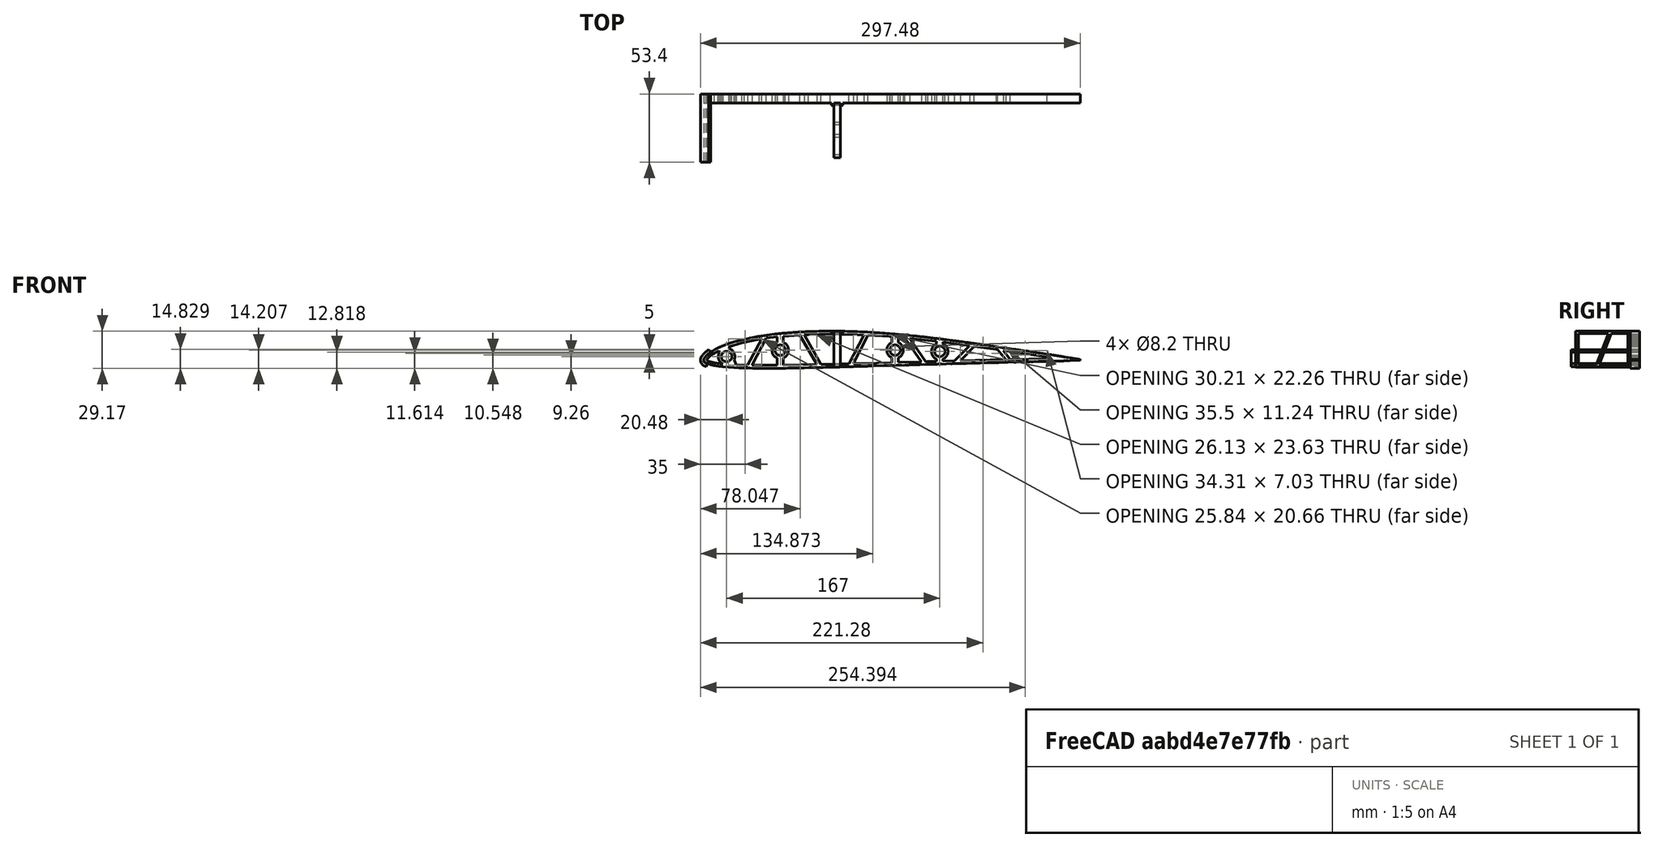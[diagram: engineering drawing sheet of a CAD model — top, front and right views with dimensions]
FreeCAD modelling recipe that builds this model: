
FCSTD DOCUMENT  (FreeCAD 1.0R39319 (Git))
Label: fpv_plane_wing
License: All rights reserved
LicenseURL: https://en.wikipedia.org/wiki/All_rights_reserved
objects: Sketcher::SketchObject×14, PartDesign::Pocket×9, PartDesign::Pad×5, Part::Part2DObjectPython×3, PartDesign::Body×3, App::DocumentObjectGroup×1, PartDesign::Thickness×1
note: 79 computed .brp shape members not serialized (recipe doc carries the construction recipe); baked Part::Feature solids carry a one-line shape summary decoded from their .brp

FEATURE [Part::Part2DObjectPython] Wire  # Draft 2D object (typed FeaturePython)
  Area = 0.0621999
  ChamferSize = 0
  Closed = true
  End = (1.00001,0,0)
  FilletRadius = 0
  Length = 2.02855
  MakeFace = true
  Placement = pos=(0,0,0) rot=(1,0,0;1.5708rad)
  Points = (61) [(1,0,0),(0.99663,0.00039,0),(0.98679,0.00172,0),(0.97104,0.00419,0),(0.94996,0.00769,0),(0.92398,0.01193,0),(0.89336,0.0167,0),(0.8584,0.02198,0),+53 more]
  Start = (1,0,0)
  Subdivisions = 0
FEATURE [Part::Part2DObjectPython] Wire002  label="wing_wire_300mm"  # Draft 2D object (typed FeaturePython)
  Area = 5597.99
  ChamferSize = 0
  Closed = true
  End = (300.003,0,0)
  FilletRadius = 0
  Length = 608.564
  MakeFace = true
  Placement = pos=(0,0,0) rot=(1,0,0;1.5708rad)
  Points = (61) [(300,0,0),(298.989,0.117,0),(296.037,0.516,0),(291.312,1.257,0),(284.988,2.307,0),(277.194,3.579,0),(268.008,5.01,0),(257.52,6.594,0),+53 more]
  Start = (300,0,0)
  Subdivisions = 0
FEATURE [App::DocumentObjectGroup] s3021
  Group = -> [Wire,Wire002]
FEATURE [Part::Part2DObjectPython] BSpline001  label="wing_wire_300mm001"  # Draft 2D object (typed FeaturePython)
  Area = 5612.28
  Closed = true
  MakeFace = true
  Parameterization = 1
  Placement = pos=(0,0,0) rot=(1,0,0;1.5708rad)
  Points = (61) [(300,0,0),(298.989,0.117,0),(296.037,0.516,0),(291.312,1.257,0),(284.988,2.307,0),(277.194,3.579,0),(268.008,5.01,0),(257.52,6.594,0),+53 more]
FEATURE [Sketcher::SketchObject] Sketch003
  ArcFitTolerance = 1e-06
  FullyConstrained = false
  MakeInternals = false
  Placement = pos=(0,0,0) rot=(1,0,0;1.5708rad)
  sketch-geometry (125):
    g0: BSplineCurve PolesCount=62 KnotsCount=62 Degree=3 IsPeriodic=1
    g1-g62: Circle [constr] x62 (B-spline internal-alignment scaffolding for g0; pole/knot coordinates omitted)
    g63-g124: GeomPoint [constr] x62 (B-spline internal-alignment scaffolding for g0; pole/knot coordinates omitted)
  constraints (125):
    c: InternalAlignment(g1,g0)
    c: Weight(g1) = 1
    c: InternalAlignment(g2,g0)
    c: Equal(g2,g1)
    c: InternalAlignment(g3,g0)
    c: Equal(g3,g1)
    c: InternalAlignment(g4,g0)
    c: Equal(g4,g1)
    c: InternalAlignment(g5,g0)
    c: Equal(g5,g1)
    c: InternalAlignment(g6,g0)
    c: Equal(g6,g1)
    c: InternalAlignment(g7,g0)
    c: Equal(g7,g1)
    c: InternalAlignment(g8,g0)
    c: Equal(g8,g1)
    c: InternalAlignment(g9,g0)
    c: Equal(g9,g1)
    c: InternalAlignment(g10,g0)
    c: Equal(g10,g1)
    c: InternalAlignment(g11,g0)
    c: Equal(g11,g1)
    c: InternalAlignment(g12,g0)
    c: Equal(g12,g1)
    c: InternalAlignment(g13,g0)
    c: Equal(g13,g1)
    c: InternalAlignment(g14,g0)
    c: Equal(g14,g1)
    c: InternalAlignment(g15,g0)
    c: Equal(g15,g1)
    c: InternalAlignment(g16,g0)
    c: Equal(g16,g1)
    c: InternalAlignment(g17,g0)
    c: Equal(g17,g1)
    c: InternalAlignment(g18,g0)
    c: Equal(g18,g1)
    c: InternalAlignment(g19,g0)
    c: Equal(g19,g1)
    c: InternalAlignment(g20,g0)
    c: Equal(g20,g1)
    c: InternalAlignment(g21,g0)
    c: Equal(g21,g1)
    c: InternalAlignment(g22,g0)
    c: Equal(g22,g1)
    c: InternalAlignment(g23,g0)
    c: Equal(g23,g1)
    c: InternalAlignment(g24,g0)
    c: Equal(g24,g1)
    c: InternalAlignment(g25,g0)
    c: Equal(g25,g1)
    c: InternalAlignment(g26,g0)
    c: Equal(g26,g1)
    c: InternalAlignment(g27,g0)
    c: Equal(g27,g1)
    c: InternalAlignment(g28,g0)
    c: Equal(g28,g1)
    c: InternalAlignment(g29,g0)
    c: Equal(g29,g1)
    c: InternalAlignment(g30,g0)
    c: Equal(g30,g1)
    c: InternalAlignment(g31,g0)
    c: Equal(g31,g1)
    c: InternalAlignment(g32,g0)
    c: Equal(g32,g1)
    c: InternalAlignment(g33,g0)
    c: Equal(g33,g1)
    c: InternalAlignment(g34,g0)
    c: Equal(g34,g1)
    c: InternalAlignment(g35,g0)
    c: Equal(g35,g1)
    c: InternalAlignment(g36,g0)
    c: Equal(g36,g1)
    c: InternalAlignment(g37,g0)
    c: Equal(g37,g1)
    c: InternalAlignment(g38,g0)
    c: Equal(g38,g1)
    c: InternalAlignment(g39,g0)
    c: Equal(g39,g1)
    c: InternalAlignment(g40,g0)
    c: Equal(g40,g1)
    c: InternalAlignment(g41,g0)
    c: Equal(g41,g1)
    c: InternalAlignment(g42,g0)
    c: Equal(g42,g1)
    c: InternalAlignment(g43,g0)
    c: Equal(g43,g1)
    c: InternalAlignment(g44,g0)
    c: Equal(g44,g1)
    c: InternalAlignment(g45,g0)
    c: Equal(g45,g1)
    c: InternalAlignment(g46,g0)
    c: Equal(g46,g1)
    c: InternalAlignment(g47,g0)
    c: Equal(g47,g1)
    c: InternalAlignment(g48,g0)
    c: Equal(g48,g1)
    c: InternalAlignment(g49,g0)
    c: Equal(g49,g1)
    c: InternalAlignment(g50,g0)
    c: Equal(g50,g1)
    c: InternalAlignment(g51,g0)
    c: Equal(g51,g1)
    c: InternalAlignment(g52,g0)
    c: Equal(g52,g1)
    c: InternalAlignment(g53,g0)
    c: Equal(g53,g1)
    c: InternalAlignment(g54,g0)
    c: Equal(g54,g1)
    c: InternalAlignment(g55,g0)
    c: Equal(g55,g1)
    c: InternalAlignment(g56,g0)
    c: Equal(g56,g1)
    c: InternalAlignment(g57,g0)
    c: Equal(g57,g1)
    c: InternalAlignment(g58,g0)
    c: Equal(g58,g1)
    c: InternalAlignment(g59,g0)
    c: Equal(g59,g1)
    c: InternalAlignment(g60,g0)
    c: Equal(g60,g1)
    c: InternalAlignment(g61,g0)
    c: Equal(g61,g1)
    c: InternalAlignment(g62,g0)
    c: Equal(g62,g1)
    c: InternalAlignment(g63-g124 -> g0) x62
FEATURE [PartDesign::Pad] Pad
  Direction = (0,-1,2e-16)
  Length = 975
  Length2 = 10
  Placement = pos=(0,0,0) rot=(1,0,0;1.5708rad)
  Profile = -> Sketch003
  ReferenceAxis = -> Sketch003 [N_Axis]
  Refine = true
  Suppressed = false
  Type = 0
FEATURE [Sketcher::SketchObject] Sketch
  ArcFitTolerance = 1e-06
  FullyConstrained = false
  MakeInternals = false
  Placement = pos=(0,0,0) rot=(1,0,0;1.5708rad)
  sketch-geometry (125):
    g0: BSplineCurve PolesCount=62 KnotsCount=62 Degree=3 IsPeriodic=1
    g1-g62: Circle [constr] x62 (B-spline internal-alignment scaffolding for g0; pole/knot coordinates omitted)
    g63-g124: GeomPoint [constr] x62 (B-spline internal-alignment scaffolding for g0; pole/knot coordinates omitted)
  constraints (125):
    c: InternalAlignment(g1,g0)
    c: Weight(g1) = 1
    c: InternalAlignment(g2,g0)
    c: Equal(g2,g1)
    c: InternalAlignment(g3,g0)
    c: Equal(g3,g1)
    c: InternalAlignment(g4,g0)
    c: Equal(g4,g1)
    c: InternalAlignment(g5,g0)
    c: Equal(g5,g1)
    c: InternalAlignment(g6,g0)
    c: Equal(g6,g1)
    c: InternalAlignment(g7,g0)
    c: Equal(g7,g1)
    c: InternalAlignment(g8,g0)
    c: Equal(g8,g1)
    c: InternalAlignment(g9,g0)
    c: Equal(g9,g1)
    c: InternalAlignment(g10,g0)
    c: Equal(g10,g1)
    c: InternalAlignment(g11,g0)
    c: Equal(g11,g1)
    c: InternalAlignment(g12,g0)
    c: Equal(g12,g1)
    c: InternalAlignment(g13,g0)
    c: Equal(g13,g1)
    c: InternalAlignment(g14,g0)
    c: Equal(g14,g1)
    c: InternalAlignment(g15,g0)
    c: Equal(g15,g1)
    c: InternalAlignment(g16,g0)
    c: Equal(g16,g1)
    c: InternalAlignment(g17,g0)
    c: Equal(g17,g1)
    c: InternalAlignment(g18,g0)
    c: Equal(g18,g1)
    c: InternalAlignment(g19,g0)
    c: Equal(g19,g1)
    c: InternalAlignment(g20,g0)
    c: Equal(g20,g1)
    c: InternalAlignment(g21,g0)
    c: Equal(g21,g1)
    c: InternalAlignment(g22,g0)
    c: Equal(g22,g1)
    c: InternalAlignment(g23,g0)
    c: Equal(g23,g1)
    c: InternalAlignment(g24,g0)
    c: Equal(g24,g1)
    c: InternalAlignment(g25,g0)
    c: Equal(g25,g1)
    c: InternalAlignment(g26,g0)
    c: Equal(g26,g1)
    c: InternalAlignment(g27,g0)
    c: Equal(g27,g1)
    c: InternalAlignment(g28,g0)
    c: Equal(g28,g1)
    c: InternalAlignment(g29,g0)
    c: Equal(g29,g1)
    c: InternalAlignment(g30,g0)
    c: Equal(g30,g1)
    c: InternalAlignment(g31,g0)
    c: Equal(g31,g1)
    c: InternalAlignment(g32,g0)
    c: Equal(g32,g1)
    c: InternalAlignment(g33,g0)
    c: Equal(g33,g1)
    c: InternalAlignment(g34,g0)
    c: Equal(g34,g1)
    c: InternalAlignment(g35,g0)
    c: Equal(g35,g1)
    c: InternalAlignment(g36,g0)
    c: Equal(g36,g1)
    c: InternalAlignment(g37,g0)
    c: Equal(g37,g1)
    c: InternalAlignment(g38,g0)
    c: Equal(g38,g1)
    c: InternalAlignment(g39,g0)
    c: Equal(g39,g1)
    c: InternalAlignment(g40,g0)
    c: Equal(g40,g1)
    c: InternalAlignment(g41,g0)
    c: Equal(g41,g1)
    c: InternalAlignment(g42,g0)
    c: Equal(g42,g1)
    c: InternalAlignment(g43,g0)
    c: Equal(g43,g1)
    c: InternalAlignment(g44,g0)
    c: Equal(g44,g1)
    c: InternalAlignment(g45,g0)
    c: Equal(g45,g1)
    c: InternalAlignment(g46,g0)
    c: Equal(g46,g1)
    c: InternalAlignment(g47,g0)
    c: Equal(g47,g1)
    c: InternalAlignment(g48,g0)
    c: Equal(g48,g1)
    c: InternalAlignment(g49,g0)
    c: Equal(g49,g1)
    c: InternalAlignment(g50,g0)
    c: Equal(g50,g1)
    c: InternalAlignment(g51,g0)
    c: Equal(g51,g1)
    c: InternalAlignment(g52,g0)
    c: Equal(g52,g1)
    c: InternalAlignment(g53,g0)
    c: Equal(g53,g1)
    c: InternalAlignment(g54,g0)
    c: Equal(g54,g1)
    c: InternalAlignment(g55,g0)
    c: Equal(g55,g1)
    c: InternalAlignment(g56,g0)
    c: Equal(g56,g1)
    c: InternalAlignment(g57,g0)
    c: Equal(g57,g1)
    c: InternalAlignment(g58,g0)
    c: Equal(g58,g1)
    c: InternalAlignment(g59,g0)
    c: Equal(g59,g1)
    c: InternalAlignment(g60,g0)
    c: Equal(g60,g1)
    c: InternalAlignment(g61,g0)
    c: Equal(g61,g1)
    c: InternalAlignment(g62,g0)
    c: Equal(g62,g1)
    c: InternalAlignment(g63-g124 -> g0) x62
FEATURE [PartDesign::Pad] Pad001
  Direction = (0,-1,2e-16)
  Length = 975
  Length2 = 10
  Placement = pos=(0,0,0) rot=(1,0,0;1.5708rad)
  Profile = -> Sketch
  ReferenceAxis = -> Sketch [N_Axis]
  Refine = true
  Suppressed = false
  Type = 0
FEATURE [Sketcher::SketchObject] Sketch004
  ArcFitTolerance = 1e-06
  AttachmentSupport = -> [XY_Plane001]
  FullyConstrained = false
  MakeInternals = false
  MapMode = 5
  sketch-geometry (4):
    g0: LineSegment StartX=299 StartY=36.1981 StartZ=0 EndX=299 EndY=-1016.06 EndZ=0
    g1: LineSegment StartX=299 StartY=-1016.06 StartZ=0 EndX=488.335 EndY=-1016.06 EndZ=0
    g2: LineSegment StartX=488.335 StartY=-1016.06 StartZ=0 EndX=488.335 EndY=36.1981 EndZ=0
    g3: LineSegment StartX=488.335 StartY=36.1981 StartZ=0 EndX=299 EndY=36.1981 EndZ=0
  constraints (9):
    c: Coincident(g0,g1)
    c: Coincident(g1,g2)
    c: Coincident(g2,g3)
    c: Coincident(g3,g0)
    c: Vertical(g0)
    c: Vertical(g2)
    c: Horizontal(g1)
    c: Horizontal(g3)
    c: DistanceX(g-1,g0) = 299
FEATURE [PartDesign::Pocket] Pocket
  BaseFeature = -> Pad001
  Direction = (0,0,-1)
  Length = 100
  Length2 = 5
  Midplane = true
  Placement = pos=(0,0,0) rot=(1,0,0;1.5708rad)
  Profile = -> Sketch004
  ReferenceAxis = -> Sketch004 [N_Axis]
  Refine = true
  Suppressed = false
  Type = 0
FEATURE [PartDesign::Thickness] Thickness
  Base = -> Pocket [Face4,Face2]
  BaseFeature = -> Pocket
  Intersection = false
  Join = 0
  Mode = 0
  Refine = true
  SupportTransform = false
  Suppressed = false
  Value = 2.5
FEATURE [Sketcher::SketchObject] Sketch005
  ArcFitTolerance = 1e-06
  AttachmentSupport = -> [Thickness]
  FullyConstrained = false
  MakeInternals = false
  MapMode = 5
  Placement = pos=(0,-975,0) rot=(1,0,0;1.5708rad)
  sketch-geometry (15):
    g0: LineSegment [constr] StartX=4.5568 StartY=5.71171 StartZ=0 EndX=7.88662 EndY=7.89278 EndZ=0
    g1: LineSegment StartX=5.46609 StartY=6.3073 StartZ=0 EndX=2.696 EndY=10.5364 EndZ=0
    g2: LineSegment StartX=2.696 StartY=10.5364 StartZ=0 EndX=32.4943 EndY=27.0739 EndZ=0
    g3: LineSegment StartX=32.4943 StartY=27.0739 StartZ=0 EndX=156.488 EndY=39.0363 EndZ=0
    g4: LineSegment StartX=156.488 StartY=39.0363 StartZ=0 EndX=248.898 EndY=26.6449 EndZ=0
    g5: LineSegment StartX=248.898 StartY=26.6449 StartZ=0 EndX=329.144 EndY=7.08029 EndZ=0
    g6: LineSegment StartX=329.144 StartY=7.08029 StartZ=0 EndX=328 EndY=-15.9084 EndZ=0
    g7: LineSegment StartX=328 StartY=-15.9084 StartZ=0 EndX=200.054 EndY=-15.9084 EndZ=0
    g8: LineSegment StartX=200.054 StartY=-15.9084 StartZ=0 EndX=64.7748 EndY=-15.9084 EndZ=0
    g9: LineSegment StartX=64.7748 StartY=-15.9084 StartZ=0 EndX=16.3454 EndY=-20.7039 EndZ=0
    g10: LineSegment StartX=16.3454 StartY=-20.7039 StartZ=0 EndX=2.88885 EndY=-12.2412 EndZ=0
    g11: LineSegment [constr] StartX=2.3291 StartY=-2.35546 StartZ=0 EndX=5.23499 EndY=-3.24958 EndZ=0
    g12: LineSegment StartX=2.88053 StartY=-2.52513 StartZ=0 EndX=1.81302 EndY=-5.99451 EndZ=0
    g13: LineSegment StartX=1.81302 StartY=-5.99451 StartZ=0 EndX=2.88885 EndY=-12.2412 EndZ=0
    g14: LineSegment StartX=5.46609 StartY=6.3073 StartZ=0 EndX=2.88053 EndY=-2.52513 EndZ=0
  constraints (22):
    c: PointOnObject(g1,g0)
    c: Perpendicular(g0,g1)
    c: Block(g1)
    c: Block(g0)
    c: Coincident(g1,g2)
    c: Coincident(g2,g3)
    c: Coincident(g3,g4)
    c: Coincident(g4,g5)
    c: Coincident(g5,g6)
    c: Coincident(g6,g7)
    c: Horizontal(g7)
    c: Coincident(g7,g8)
    c: Horizontal(g8)
    c: Coincident(g8,g9)
    c: Coincident(g9,g10)
    c: Block(g11)
    c: PointOnObject(g12,g11)
    c: Perpendicular(g11,g12)
    c: Coincident(g13,g12)
    c: Coincident(g13,g10)
    c: Coincident(g14,g1)
    c: Coincident(g14,g12)
FEATURE [PartDesign::Pocket] Pocket001
  BaseFeature = -> Thickness
  Direction = (0,1,-2e-16)
  Length = 1000
  Length2 = 5
  Profile = -> Sketch005
  ReferenceAxis = -> Sketch005 [N_Axis]
  Refine = true
  Suppressed = false
  Type = 0
FEATURE [Sketcher::SketchObject] Sketch006
  ArcFitTolerance = 1e-06
  AttachmentSupport = -> [Pad]
  FullyConstrained = false
  MakeInternals = false
  MapMode = 5
  Placement = pos=(0,-975,0) rot=(1,0,0;1.5708rad)
  sketch-geometry (29):
    g0: LineSegment StartX=2.71326 StartY=0.775372 StartZ=0 EndX=3.3867 EndY=1.52303 EndZ=0
    g1: LineSegment StartX=3.3867 StartY=1.52303 StartZ=0 EndX=5.99321 EndY=4.17962 EndZ=0
    g2: LineSegment StartX=5.99321 StartY=4.17962 StartZ=0 EndX=11.2308 EndY=7.18071 EndZ=0
    g3: LineSegment StartX=11.2308 StartY=7.18071 StartZ=0 EndX=18.9287 EndY=10.4927 EndZ=0
    g4: LineSegment StartX=18.9287 StartY=10.4927 StartZ=0 EndX=30.0156 EndY=13.8045 EndZ=0
    g5: LineSegment StartX=30.0156 StartY=13.8045 StartZ=0 EndX=43.7053 EndY=16.6585 EndZ=0
    g6: LineSegment StartX=43.7053 StartY=16.6585 StartZ=0 EndX=58.3753 EndY=18.5837 EndZ=0
    g7: LineSegment StartX=58.3753 StartY=18.5837 StartZ=0 EndX=81.9328 EndY=20.1998 EndZ=0
    g8: LineSegment StartX=81.9328 StartY=20.1998 StartZ=0 EndX=99.116 EndY=20.5815 EndZ=0
    g9: LineSegment StartX=99.116 StartY=20.5815 StartZ=0 EndX=120.506 EndY=20.1998 EndZ=0
    g10: LineSegment StartX=120.506 StartY=20.1998 StartZ=0 EndX=145.772 EndY=18.6559 EndZ=0
    g11: LineSegment StartX=145.772 StartY=18.6559 StartZ=0 EndX=175.748 EndY=15.7728 EndZ=0
    g12: LineSegment StartX=175.748 StartY=15.7728 StartZ=0 EndX=200.436 EndY=12.5699 EndZ=0
    g13: LineSegment StartX=200.436 StartY=12.5699 StartZ=0 EndX=229.384 EndY=8.60252 EndZ=0
    g14: LineSegment StartX=229.384 StartY=8.60252 StartZ=0 EndX=252.135 EndY=5.21302 EndZ=0
    g15: LineSegment StartX=252.135 StartY=5.21302 StartZ=0 EndX=269.07 EndY=2.67143 EndZ=0
    g16: LineSegment StartX=269.07 StartY=2.67143 StartZ=0 EndX=269.07 EndY=1.39956 EndZ=0
    g17: LineSegment StartX=269.07 StartY=1.39956 StartZ=0 EndX=224.761 EndY=0.436598 EndZ=0
    g18: LineSegment StartX=224.761 StartY=0.436598 StartZ=0 EndX=175.487 EndY=-1.02731 EndZ=0
    g19: LineSegment StartX=175.487 StartY=-1.02731 StartZ=0 EndX=123.478 EndY=-2.41293 EndZ=0
    g20: LineSegment StartX=123.478 StartY=-2.41293 StartZ=0 EndX=62.0775 EndY=-3.87655 EndZ=0
    g21: LineSegment StartX=62.0775 StartY=-3.87655 StartZ=0 EndX=32.0529 EndY=-3.76091 EndZ=0
    g22: LineSegment StartX=32.0529 StartY=-3.76091 StartZ=0 EndX=18.888 EndY=-3.18288 EndZ=0
    g23: LineSegment StartX=18.888 StartY=-3.18288 StartZ=0 EndX=12.7286 EndY=-2.48971 EndZ=0
    g24: LineSegment StartX=12.7286 StartY=-2.48971 StartZ=0 EndX=8.49342 EndY=-1.8722 EndZ=0
    g25: LineSegment StartX=8.49342 StartY=-1.8722 StartZ=0 EndX=4.56236 EndY=-0.768246 EndZ=0
    g26: LineSegment StartX=4.56236 StartY=-0.768246 StartZ=0 EndX=3.01395 EndY=-0.301296 EndZ=0
    g27: ArcOfCircle CenterX=3.20505 CenterY=0.332397 CenterZ=0 NormalX=0 NormalY=0 NormalZ=1 AngleXU=0 Radius=0.661881 StartAngle=2.40837 EndAngle=4.41949
    g28: GeomPoint [constr] X=2.01486 Y=0 Z=0
  constraints (32):
    c: PointOnObject(g28,g-1)
    c: Coincident(g0,g1)
    c: Coincident(g1,g2)
    c: Coincident(g2,g3)
    c: Coincident(g3,g4)
    c: Coincident(g4,g5)
    c: Coincident(g5,g6)
    c: Coincident(g6,g7)
    c: Coincident(g7,g8)
    c: Coincident(g8,g9)
    c: Coincident(g9,g10)
    c: Coincident(g10,g11)
    c: Coincident(g11,g12)
    c: Coincident(g12,g13)
    c: Coincident(g13,g14)
    c: Coincident(g14,g15)
    c: Coincident(g15,g16)
    c: Vertical(g16)
    c: Coincident(g16,g17)
    c: Coincident(g17,g18)
    c: Coincident(g18,g19)
    c: Coincident(g19,g20)
    c: Coincident(g20,g21)
    c: Coincident(g21,g22)
    c: Coincident(g22,g23)
    c: Coincident(g23,g24)
    c: Coincident(g24,g25)
    c: Coincident(g25,g26)
    c: PointOnObject(g28,g0)
    c: PointOnObject(g28,g26)
    c: Tangent(g0,g27) = 1.5708
    c: Tangent(g26,g27) = 1.5708
FEATURE [PartDesign::Pocket] Pocket002
  BaseFeature = -> Pad
  Direction = (0,1,-2e-16)
  Length = 1000
  Length2 = 5
  Placement = pos=(0,0,0) rot=(1,0,0;1.5708rad)
  Profile = -> Sketch006
  ReferenceAxis = -> Sketch006 [N_Axis]
  Refine = true
  Suppressed = false
  Type = 0
FEATURE [Sketcher::SketchObject] Sketch007
  ArcFitTolerance = 1e-06
  AttachmentSupport = -> [XY_Plane]
  FullyConstrained = false
  MakeInternals = false
  MapMode = 5
  sketch-geometry (4):
    g0: LineSegment StartX=295 StartY=17.3691 StartZ=0 EndX=295 EndY=-1072.59 EndZ=0
    g1: LineSegment StartX=295 StartY=-1072.59 StartZ=0 EndX=384.545 EndY=-1072.59 EndZ=0
    g2: LineSegment StartX=384.545 StartY=-1072.59 StartZ=0 EndX=384.545 EndY=17.3691 EndZ=0
    g3: LineSegment StartX=384.545 StartY=17.3691 StartZ=0 EndX=295 EndY=17.3691 EndZ=0
  constraints (9):
    c: Coincident(g0,g1)
    c: Coincident(g1,g2)
    c: Coincident(g2,g3)
    c: Coincident(g3,g0)
    c: Vertical(g0)
    c: Vertical(g2)
    c: Horizontal(g1)
    c: Horizontal(g3)
    c: DistanceX(g-1,g0) = 295
FEATURE [PartDesign::Pocket] Pocket003
  BaseFeature = -> Pocket002
  Direction = (0,0,-1)
  Length = 5
  Length2 = 5
  Midplane = true
  Placement = pos=(0,0,0) rot=(1,0,0;1.5708rad)
  Profile = -> Sketch007
  ReferenceAxis = -> Sketch007 [N_Axis]
  Refine = true
  Suppressed = false
  Type = 0
FEATURE [Sketcher::SketchObject] Sketch008
  ArcFitTolerance = 1e-06
  AttachmentSupport = -> [Pocket003]
  FullyConstrained = false
  MakeInternals = false
  MapMode = 5
  Placement = pos=(0,-975,0) rot=(1,0,0;1.5708rad)
  sketch-geometry (60):
    g0: LineSegment StartX=45.884 StartY=17.7219 StartZ=0 EndX=33.93 EndY=-4.65497 EndZ=0
    g1: LineSegment StartX=49.8645 StartY=18.8062 StartZ=0 EndX=37.3312 EndY=-4.65497 EndZ=0
    g2: LineSegment StartX=45.884 StartY=17.7219 StartZ=0 EndX=49.8645 EndY=18.8062 EndZ=0
    g3: LineSegment StartX=33.93 StartY=-4.65497 StartZ=0 EndX=37.3312 EndY=-4.65497 EndZ=0
    g4: ArcOfCircle CenterX=18 CenterY=3 CenterZ=0 NormalX=0 NormalY=0 NormalZ=1 AngleXU=0 Radius=6.5 StartAngle=2.58175 EndAngle=4.38597
    g5: LineSegment StartX=20.6963 StartY=8.91437 StartZ=0 EndX=19.1912 EndY=11.3613 EndZ=0
    g6: LineSegment StartX=12.4923 StartY=6.45183 StartZ=0 EndX=11.7252 EndY=8.2111 EndZ=0
    g7: LineSegment StartX=11.7252 StartY=8.2111 StartZ=0 EndX=19.1912 EndY=11.3613 EndZ=0
    g8: LineSegment StartX=23.9272 StartY=0.331954 StartZ=0 EndX=26.093 EndY=-4.58272 EndZ=0
    g9: LineSegment StartX=15.9158 StartY=-3.15679 StartZ=0 EndX=16.6159 EndY=-4.58272 EndZ=0
    g10: LineSegment StartX=16.6159 StartY=-4.58272 StartZ=0 EndX=26.093 EndY=-4.58272 EndZ=0
    g11: LineSegment StartX=74.8373 StartY=20.9684 StartZ=0 EndX=89.2063 EndY=-4.24973 EndZ=0
    g12: LineSegment StartX=89.2063 StartY=-4.24973 StartZ=0 EndX=92.6591 EndY=-4.24973 EndZ=0
    g13: LineSegment StartX=92.6591 StartY=-4.24973 StartZ=0 EndX=78.184 EndY=21.1546 EndZ=0
    g14: LineSegment StartX=78.184 StartY=21.1546 StartZ=0 EndX=74.8373 EndY=20.9684 EndZ=0
    g15: LineSegment StartX=113.372 StartY=-3.61742 StartZ=0 EndX=125.992 EndY=20.9865 EndZ=0
    g16: LineSegment StartX=125.992 StartY=20.9865 StartZ=0 EndX=129.338 EndY=20.9348 EndZ=0
    g17: LineSegment StartX=129.338 StartY=20.9348 StartZ=0 EndX=116.743 EndY=-3.61742 EndZ=0
    g18: LineSegment StartX=116.743 StartY=-3.61742 StartZ=0 EndX=113.372 EndY=-3.61742 EndZ=0
    g19: LineSegment StartX=156.49 StartY=19.0126 StartZ=0 EndX=171.224 EndY=-2.18705 EndZ=0
    g20: LineSegment StartX=171.224 StartY=-2.18705 StartZ=0 EndX=175.064 EndY=-2.45586 EndZ=0
    g21: LineSegment StartX=175.064 StartY=-2.45586 StartZ=0 EndX=160.386 EndY=18.6636 EndZ=0
    g22: LineSegment StartX=160.386 StartY=18.6636 StartZ=0 EndX=156.49 EndY=19.0126 EndZ=0
    g23: LineSegment StartX=195.991 StartY=-1.14503 StartZ=0 EndX=209.19 EndY=12.3205 EndZ=0
    g24: LineSegment StartX=209.19 StartY=12.3205 StartZ=0 EndX=213.44 EndY=12.3702 EndZ=0
    g25: LineSegment StartX=213.44 StartY=12.3702 StartZ=0 EndX=200.192 EndY=-1.14503 EndZ=0
    g26: LineSegment StartX=200.192 StartY=-1.14503 StartZ=0 EndX=195.991 EndY=-1.14503 EndZ=0
    g27: LineSegment StartX=229.838 StartY=9.19446 StartZ=0 EndX=237.096 EndY=0 EndZ=0
    g28: LineSegment StartX=237.096 StartY=0 StartZ=0 EndX=240.918 EndY=0 EndZ=0
    g29: LineSegment StartX=240.918 StartY=0 StartZ=0 EndX=234.226 EndY=8.47688 EndZ=0
    g30: LineSegment StartX=234.226 StartY=8.47688 StartZ=0 EndX=229.838 EndY=9.19446 EndZ=0
    g31: ArcOfCircle CenterX=18 CenterY=3 CenterZ=0 NormalX=0 NormalY=0 NormalZ=1 AngleXU=0 Radius=6.5 StartAngle=5.86022 EndAngle=7.42624
    g32: Circle CenterX=18 CenterY=3 CenterZ=0 NormalX=0 NormalY=0 NormalZ=1 AngleXU=0 Radius=4.1
    g33: Circle CenterX=60 CenterY=8 CenterZ=0 NormalX=0 NormalY=0 NormalZ=1 AngleXU=0 Radius=4.1
    g34: Circle CenterX=150 CenterY=8 CenterZ=0 NormalX=0 NormalY=0 NormalZ=1 AngleXU=0 Radius=4.1
    g35: ArcOfCircle CenterX=60 CenterY=8 CenterZ=0 NormalX=0 NormalY=0 NormalZ=1 AngleXU=0 Radius=6.5 StartAngle=1.96559 EndAngle=4.3176
    g36: Circle CenterX=185 CenterY=7 CenterZ=0 NormalX=0 NormalY=0 NormalZ=1 AngleXU=0 Radius=4.1
    g37: LineSegment StartX=57.5 StartY=14 StartZ=0 EndX=57.5 EndY=19.5561 EndZ=0
    g38: LineSegment StartX=62.5 StartY=14 StartZ=0 EndX=62.5 EndY=20.0342 EndZ=0
    g39: LineSegment StartX=62.5 StartY=20.0342 StartZ=0 EndX=57.5 EndY=19.5561 EndZ=0
    g40: LineSegment StartX=57.5 StartY=2 StartZ=0 EndX=57.5 EndY=-4.90591 EndZ=0
    g41: LineSegment StartX=57.5 StartY=-4.90591 StartZ=0 EndX=62.5 EndY=-4.90591 EndZ=0
    g42: LineSegment StartX=62.5 StartY=-4.90591 StartZ=0 EndX=62.5 EndY=2 EndZ=0
    g43: ArcOfCircle CenterX=60 CenterY=8 CenterZ=0 NormalX=0 NormalY=0 NormalZ=1 AngleXU=0 Radius=6.5 StartAngle=5.10718 EndAngle=7.45919
    g44: ArcOfCircle CenterX=150 CenterY=8 CenterZ=0 NormalX=0 NormalY=0 NormalZ=1 AngleXU=0 Radius=6.5 StartAngle=1.96559 EndAngle=4.3176
    g45: ArcOfCircle CenterX=185 CenterY=7 CenterZ=0 NormalX=0 NormalY=0 NormalZ=1 AngleXU=0 Radius=6.5 StartAngle=1.96559 EndAngle=4.3176
    g46: LineSegment StartX=147.5 StartY=14 StartZ=0 EndX=147.5 EndY=19.2414 EndZ=0
    g47: LineSegment StartX=147.5 StartY=19.2414 StartZ=0 EndX=152.5 EndY=18.961 EndZ=0
    g48: LineSegment StartX=152.5 StartY=18.961 StartZ=0 EndX=152.5 EndY=14 EndZ=0
    g49: LineSegment StartX=147.5 StartY=2 StartZ=0 EndX=147.5 EndY=-2.5624 EndZ=0
    g50: LineSegment StartX=147.5 StartY=-2.5624 StartZ=0 EndX=152.5 EndY=-2.5624 EndZ=0
    g51: LineSegment StartX=152.5 StartY=-2.5624 StartZ=0 EndX=152.5 EndY=2 EndZ=0
    g52: ArcOfCircle CenterX=150 CenterY=8 CenterZ=0 NormalX=0 NormalY=0 NormalZ=1 AngleXU=0 Radius=6.5 StartAngle=5.10718 EndAngle=7.45919
    g53: LineSegment StartX=182.5 StartY=13 StartZ=0 EndX=182.5 EndY=15.9367 EndZ=0
    g54: LineSegment StartX=182.5 StartY=15.9367 StartZ=0 EndX=187.5 EndY=15.5349 EndZ=0
    g55: LineSegment StartX=187.5 StartY=15.5349 StartZ=0 EndX=187.5 EndY=13 EndZ=0
    g56: LineSegment StartX=182.5 StartY=1 StartZ=0 EndX=182.5 EndY=-1.79994 EndZ=0
    g57: LineSegment StartX=182.5 StartY=-1.79994 StartZ=0 EndX=187.5 EndY=-1.79994 EndZ=0
    g58: LineSegment StartX=187.5 StartY=-1.79994 StartZ=0 EndX=187.5 EndY=1 EndZ=0
    g59: ArcOfCircle CenterX=185 CenterY=7 CenterZ=0 NormalX=0 NormalY=0 NormalZ=1 AngleXU=0 Radius=6.5 StartAngle=5.10718 EndAngle=7.45919
  constraints (134):
    c: Coincident(g2,g0)
    c: Coincident(g2,g1)
    c: Coincident(g3,g0)
    c: Coincident(g3,g1)
    c: Horizontal(g3)
    c: Parallel(g0,g1)
    c: Distance(g1,g0) = 3
    c: Diameter(g4) = 13
    c: DistanceY(g-1,g4) = 3
    c: DistanceX(g-1,g4) = 18
    c: Coincident(g7,g6)
    c: Coincident(g7,g5)
    c: PointOnObject(g8,g31)
    c: Coincident(g10,g9)
    c: Horizontal(g10)
    c: Coincident(g10,g8)
    c: Coincident(g11,g12)
    c: Horizontal(g12)
    c: Coincident(g12,g13)
    c: Coincident(g13,g14)
    c: Coincident(g14,g11)
    c: Parallel(g11,g13)
    c: Distance(g13,g11) = 3
    c: Coincident(g15,g16)
    c: Coincident(g16,g17)
    c: Coincident(g17,g18)
    c: Coincident(g18,g15)
    c: Horizontal(g18)
    c: Parallel(g17,g15)
    c: Distance(g17,g15) = 3
    c: Coincident(g19,g20)
    c: Coincident(g20,g21)
    c: Coincident(g21,g22)
    c: Coincident(g22,g19)
    c: Parallel(g19,g21)
    c: Distance(g21,g19) = 3
    c: Coincident(g23,g24)
    c: Coincident(g24,g25)
    c: Coincident(g25,g26)
    c: Horizontal(g26)
    c: Parallel(g23,g25)
    c: Distance(g25,g23) = 3
    c: PointOnObject(g27,g-1)
    c: Coincident(g27,g28)
    c: PointOnObject(g28,g-1)
    c: Coincident(g28,g29)
    c: Coincident(g29,g30)
    c: Coincident(g30,g27)
    c: Parallel(g27,g29)
    c: Distance(g29,g27) = 3
    c: Coincident(g31,g5)
    c: Coincident(g4,g6)
    c: Equal(g4,g31)
    c: Coincident(g4,g9)
    c: PointOnObject(g31,g8)
    c: Coincident(g4,g31)
    c: Coincident(g26,g23)
    c: Diameter(g32) = 8.2
    c: Coincident(g32,g4)
    c: Diameter(g33) = 8.2
    c: Diameter(g34) = 8.2
    c: DistanceX(g33,g34) = 90
    c: Coincident(g35,g33)
    c: Diameter(g35) = 13
    c: DistanceX(g-1,g33) = 60
    c: DistanceY(g-1,g33) = 8
    c: DistanceY(g-1,g34) = 8
    c: Diameter(g36) = 8.2
    c: DistanceY(g-1,g36) = 7
    c: DistanceX(g-1,g36) = 185
    c: Vertical(g37)
    c: Vertical(g38)
    c: Coincident(g39,g38)
    c: Coincident(g39,g37)
    c: Distance(g38,g37) = 5
    c: DistanceX(g37,g33) = 2.5
    c: Coincident(g40,g41)
    c: Horizontal(g41)
    c: Coincident(g41,g42)
    c: PointOnObject(g42,g43)
    c: Vertical(g40)
    c: Vertical(g42)
    c: DistanceX(g40,g33) = 2.5
    c: DistanceX(g41,g41) = 5
    c: Coincident(g43,g38)
    c: Coincident(g35,g37)
    c: Equal(g35,g43)
    c: Coincident(g35,g40)
    c: PointOnObject(g43,g42)
    c: Coincident(g35,g43)
    c: Diameter(g44) = 13
    c: Coincident(g44,g34)
    c: Diameter(g45) = 13
    c: Coincident(g45,g36)
    c: Vertical(g46)
    c: Coincident(g46,g47)
    c: Coincident(g47,g48)
    c: Vertical(g48)
    c: Vertical(g49)
    c: Coincident(g49,g50)
    c: Horizontal(g50)
    c: Coincident(g50,g51)
    c: PointOnObject(g51,g52)
    c: Vertical(g51)
    c: DistanceX(g50,g50) = 5
    c: DistanceX(g49,g34) = 2.5
    c: Distance(g48,g46) = 5
    c: DistanceX(g46,g34) = 2.5
    c: Coincident(g52,g48)
    c: Coincident(g44,g46)
    c: Equal(g44,g52)
    c: Coincident(g44,g49)
    c: PointOnObject(g52,g51)
    c: Coincident(g44,g52)
    c: Coincident(g53,g54)
    c: Coincident(g54,g55)
    c: Vertical(g55)
    c: Vertical(g56)
    c: Coincident(g56,g57)
    c: Horizontal(g57)
    c: Coincident(g57,g58)
    c: PointOnObject(g58,g59)
    c: Vertical(g58)
    c: Vertical(g53)
    c: Distance(g55,g53) = 5
    c: DistanceX(g53,g36) = 2.5
    c: Distance(g56,g58) = 5
    c: DistanceX(g56,g36) = 2.5
    c: Coincident(g59,g55)
    c: Coincident(g45,g53)
    c: Equal(g45,g59)
    c: Coincident(g45,g56)
    c: PointOnObject(g59,g58)
    c: Coincident(g45,g59)
FEATURE [PartDesign::Pad] Pad002
  BaseFeature = -> Pocket003
  Direction = (0,-1,2e-16)
  Length = 975
  Length2 = 10
  Placement = pos=(0,0,0) rot=(1,0,0;1.5708rad)
  Profile = -> Sketch008
  ReferenceAxis = -> Sketch008 [N_Axis]
  Refine = true
  Reversed = true
  Suppressed = false
  Type = 0
FEATURE [Sketcher::SketchObject] Sketch009
  ArcFitTolerance = 1e-06
  AttachmentSupport = -> [XY_Plane]
  FullyConstrained = false
  MakeInternals = false
  MapMode = 5
  sketch-geometry (4):
    g0: LineSegment StartX=-107.72 StartY=-9 StartZ=0 EndX=-107.72 EndY=-997.777 EndZ=0
    g1: LineSegment StartX=-107.72 StartY=-997.777 StartZ=0 EndX=422.62 EndY=-997.777 EndZ=0
    g2: LineSegment StartX=422.62 StartY=-997.777 StartZ=0 EndX=422.62 EndY=-9 EndZ=0
    g3: LineSegment StartX=422.62 StartY=-9 StartZ=0 EndX=-107.72 EndY=-9 EndZ=0
  constraints (9):
    c: Coincident(g0,g1)
    c: Coincident(g1,g2)
    c: Coincident(g2,g3)
    c: Coincident(g3,g0)
    c: Vertical(g0)
    c: Vertical(g2)
    c: Horizontal(g1)
    c: Horizontal(g3)
    c: DistanceY(g0,g-1) = 9
FEATURE [PartDesign::Pocket] Pocket004
  BaseFeature = -> Pad002
  Direction = (0,0,-1)
  Length = 100
  Length2 = 5
  Midplane = true
  Placement = pos=(0,0,0) rot=(1,0,0;1.5708rad)
  Profile = -> Sketch009
  ReferenceAxis = -> Sketch009 [N_Axis]
  Refine = true
  Suppressed = false
  Type = 0
FEATURE [Sketcher::SketchObject] Sketch010
  ArcFitTolerance = 1e-06
  AttachmentSupport = -> [XY_Plane001]
  FullyConstrained = false
  MakeInternals = false
  MapMode = 5
  sketch-geometry (4):
    g0: LineSegment StartX=-58.8398 StartY=-1038.33 StartZ=0 EndX=102.633 EndY=-1038.33 EndZ=0
    g1: LineSegment StartX=102.633 StartY=-1038.33 StartZ=0 EndX=102.633 EndY=-53.4 EndZ=0
    g2: LineSegment StartX=102.633 StartY=-53.4 StartZ=0 EndX=-58.8398 EndY=-53.4 EndZ=0
    g3: LineSegment StartX=-58.8398 StartY=-53.4 StartZ=0 EndX=-58.8398 EndY=-1038.33 EndZ=0
  constraints (9):
    c: Coincident(g0,g1)
    c: Coincident(g1,g2)
    c: Coincident(g2,g3)
    c: Coincident(g3,g0)
    c: Horizontal(g0)
    c: Horizontal(g2)
    c: Vertical(g1)
    c: Vertical(g3)
    c: DistanceY(g2,g-1) = 53.4
FEATURE [PartDesign::Pocket] Pocket005
  BaseFeature = -> Pocket001
  Direction = (0,0,-1)
  Length = 100
  Length2 = 5
  Midplane = true
  Profile = -> Sketch010
  ReferenceAxis = -> Sketch010 [N_Axis]
  Refine = true
  Suppressed = false
  Type = 0
FEATURE [PartDesign::Body] Body001  label="leading edge"
  AllowCompound = false
  Group = -> [Sketch,Pad001,Sketch004,Pocket,Thickness,Sketch005,Pocket001,Sketch010,Pocket005]
  Origin = -> Origin001
  Tip = -> Pocket005
FEATURE [Sketcher::SketchObject] Sketch011
  ArcFitTolerance = 1e-06
  AttachmentSupport = -> [Pocket004]
  FullyConstrained = false
  MakeInternals = false
  MapMode = 5
  Placement = pos=(0,-9,-3e-15) rot=(1,0,0;1.5708rad)
  sketch-geometry (12):
    g0: LineSegment StartX=-10.975 StartY=36.8853 StartZ=0 EndX=-10.975 EndY=-12.6675 EndZ=0
    g1: LineSegment StartX=-10.975 StartY=-12.6675 StartZ=0 EndX=100 EndY=-12.6675 EndZ=0
    g2: LineSegment StartX=100 StartY=-12.6675 StartZ=0 EndX=100 EndY=36.8853 EndZ=0
    g3: LineSegment StartX=100 StartY=36.8853 StartZ=0 EndX=-10.975 EndY=36.8853 EndZ=0
    g4: LineSegment StartX=102 StartY=39.5582 StartZ=0 EndX=102 EndY=-18.5722 EndZ=0
    g5: LineSegment StartX=102 StartY=-18.5722 StartZ=0 EndX=107.1 EndY=-18.5722 EndZ=0
    g6: LineSegment StartX=107.1 StartY=-18.5722 StartZ=0 EndX=107.1 EndY=39.5582 EndZ=0
    g7: LineSegment StartX=107.1 StartY=39.5582 StartZ=0 EndX=102 EndY=39.5582 EndZ=0
    g8: LineSegment StartX=109.1 StartY=30.6012 StartZ=0 EndX=109.1 EndY=-14.7558 EndZ=0
    g9: LineSegment StartX=109.1 StartY=-14.7558 StartZ=0 EndX=312.078 EndY=-14.7558 EndZ=0
    g10: LineSegment StartX=312.078 StartY=-14.7558 StartZ=0 EndX=312.078 EndY=30.6012 EndZ=0
    g11: LineSegment StartX=312.078 StartY=30.6012 StartZ=0 EndX=109.1 EndY=30.6012 EndZ=0
  constraints (28):
    c: Coincident(g0,g1)
    c: Coincident(g1,g2)
    c: Coincident(g2,g3)
    c: Coincident(g3,g0)
    c: Vertical(g0)
    c: Vertical(g2)
    c: Horizontal(g1)
    c: Horizontal(g3)
    c: Coincident(g4,g5)
    c: Coincident(g5,g6)
    c: Coincident(g6,g7)
    c: Coincident(g7,g4)
    c: Vertical(g4)
    c: Vertical(g6)
    c: Horizontal(g5)
    c: Horizontal(g7)
    c: Coincident(g8,g9)
    c: Coincident(g9,g10)
    c: Coincident(g10,g11)
    c: Coincident(g11,g8)
    c: Vertical(g8)
    c: Vertical(g10)
    c: Horizontal(g9)
    c: Horizontal(g11)
    c: DistanceX(g-1,g2) = 100
    c: DistanceX(g2,g4) = 2
    c: DistanceX(g7,g7) = 5.1
    c: DistanceX(g6,g8) = 2
FEATURE [PartDesign::Pocket] Pocket006
  BaseFeature = -> Pocket004
  Direction = (0,1,-2e-16)
  Length = 2
  Length2 = 5
  Placement = pos=(0,0,0) rot=(1,0,0;1.5708rad)
  Profile = -> Sketch011
  ReferenceAxis = -> Sketch011 [N_Axis]
  Refine = true
  Suppressed = false
  Type = 0
FEATURE [PartDesign::Body] Body  label="wingspar 1"
  AllowCompound = false
  Group = -> [Sketch003,Pad,Sketch006,Pocket002,Sketch007,Pocket003,Sketch008,Pad002,Sketch009,Pocket004,Sketch011,Pocket006]
  Origin = -> Origin
  Tip = -> Pocket006
FEATURE [Sketcher::SketchObject] Sketch012
  ArcFitTolerance = 1e-06
  FullyConstrained = false
  MakeInternals = false
  Placement = pos=(0,0,0) rot=(1,0,0;1.5708rad)
  sketch-geometry (125):
    g0: BSplineCurve PolesCount=62 KnotsCount=62 Degree=3 IsPeriodic=1
    g1-g62: Circle [constr] x62 (B-spline internal-alignment scaffolding for g0; pole/knot coordinates omitted)
    g63-g124: GeomPoint [constr] x62 (B-spline internal-alignment scaffolding for g0; pole/knot coordinates omitted)
  constraints (125):
    c: InternalAlignment(g1,g0)
    c: Weight(g1) = 1
    c: InternalAlignment(g2,g0)
    c: Equal(g2,g1)
    c: InternalAlignment(g3,g0)
    c: Equal(g3,g1)
    c: InternalAlignment(g4,g0)
    c: Equal(g4,g1)
    c: InternalAlignment(g5,g0)
    c: Equal(g5,g1)
    c: InternalAlignment(g6,g0)
    c: Equal(g6,g1)
    c: InternalAlignment(g7,g0)
    c: Equal(g7,g1)
    c: InternalAlignment(g8,g0)
    c: Equal(g8,g1)
    c: InternalAlignment(g9,g0)
    c: Equal(g9,g1)
    c: InternalAlignment(g10,g0)
    c: Equal(g10,g1)
    c: InternalAlignment(g11,g0)
    c: Equal(g11,g1)
    c: InternalAlignment(g12,g0)
    c: Equal(g12,g1)
    c: InternalAlignment(g13,g0)
    c: Equal(g13,g1)
    c: InternalAlignment(g14,g0)
    c: Equal(g14,g1)
    c: InternalAlignment(g15,g0)
    c: Equal(g15,g1)
    c: InternalAlignment(g16,g0)
    c: Equal(g16,g1)
    c: InternalAlignment(g17,g0)
    c: Equal(g17,g1)
    c: InternalAlignment(g18,g0)
    c: Equal(g18,g1)
    c: InternalAlignment(g19,g0)
    c: Equal(g19,g1)
    c: InternalAlignment(g20,g0)
    c: Equal(g20,g1)
    c: InternalAlignment(g21,g0)
    c: Equal(g21,g1)
    c: InternalAlignment(g22,g0)
    c: Equal(g22,g1)
    c: InternalAlignment(g23,g0)
    c: Equal(g23,g1)
    c: InternalAlignment(g24,g0)
    c: Equal(g24,g1)
    c: InternalAlignment(g25,g0)
    c: Equal(g25,g1)
    c: InternalAlignment(g26,g0)
    c: Equal(g26,g1)
    c: InternalAlignment(g27,g0)
    c: Equal(g27,g1)
    c: InternalAlignment(g28,g0)
    c: Equal(g28,g1)
    c: InternalAlignment(g29,g0)
    c: Equal(g29,g1)
    c: InternalAlignment(g30,g0)
    c: Equal(g30,g1)
    c: InternalAlignment(g31,g0)
    c: Equal(g31,g1)
    c: InternalAlignment(g32,g0)
    c: Equal(g32,g1)
    c: InternalAlignment(g33,g0)
    c: Equal(g33,g1)
    c: InternalAlignment(g34,g0)
    c: Equal(g34,g1)
    c: InternalAlignment(g35,g0)
    c: Equal(g35,g1)
    c: InternalAlignment(g36,g0)
    c: Equal(g36,g1)
    c: InternalAlignment(g37,g0)
    c: Equal(g37,g1)
    c: InternalAlignment(g38,g0)
    c: Equal(g38,g1)
    c: InternalAlignment(g39,g0)
    c: Equal(g39,g1)
    c: InternalAlignment(g40,g0)
    c: Equal(g40,g1)
    c: InternalAlignment(g41,g0)
    c: Equal(g41,g1)
    c: InternalAlignment(g42,g0)
    c: Equal(g42,g1)
    c: InternalAlignment(g43,g0)
    c: Equal(g43,g1)
    c: InternalAlignment(g44,g0)
    c: Equal(g44,g1)
    c: InternalAlignment(g45,g0)
    c: Equal(g45,g1)
    c: InternalAlignment(g46,g0)
    c: Equal(g46,g1)
    c: InternalAlignment(g47,g0)
    c: Equal(g47,g1)
    c: InternalAlignment(g48,g0)
    c: Equal(g48,g1)
    c: InternalAlignment(g49,g0)
    c: Equal(g49,g1)
    c: InternalAlignment(g50,g0)
    c: Equal(g50,g1)
    c: InternalAlignment(g51,g0)
    c: Equal(g51,g1)
    c: InternalAlignment(g52,g0)
    c: Equal(g52,g1)
    c: InternalAlignment(g53,g0)
    c: Equal(g53,g1)
    c: InternalAlignment(g54,g0)
    c: Equal(g54,g1)
    c: InternalAlignment(g55,g0)
    c: Equal(g55,g1)
    c: InternalAlignment(g56,g0)
    c: Equal(g56,g1)
    c: InternalAlignment(g57,g0)
    c: Equal(g57,g1)
    c: InternalAlignment(g58,g0)
    c: Equal(g58,g1)
    c: InternalAlignment(g59,g0)
    c: Equal(g59,g1)
    c: InternalAlignment(g60,g0)
    c: Equal(g60,g1)
    c: InternalAlignment(g61,g0)
    c: Equal(g61,g1)
    c: InternalAlignment(g62,g0)
    c: Equal(g62,g1)
    c: InternalAlignment(g63-g124 -> g0) x62
FEATURE [PartDesign::Pad] Pad003
  Direction = (0,-1,2e-16)
  Length = 975
  Length2 = 10
  Placement = pos=(0,0,0) rot=(1,0,0;1.5708rad)
  Profile = -> Sketch012
  ReferenceAxis = -> Sketch012 [N_Axis]
  Refine = true
  Suppressed = false
  Type = 0
FEATURE [Sketcher::SketchObject] Sketch013
  ArcFitTolerance = 1e-06
  AttachmentSupport = -> [XY_Plane002]
  FullyConstrained = true
  MakeInternals = false
  MapMode = 5
  sketch-geometry (8):
    g0: LineSegment StartX=0 StartY=0 StartZ=0 EndX=0 EndY=-1100 EndZ=0
    g1: LineSegment StartX=0 StartY=-1100 StartZ=0 EndX=310 EndY=-1100 EndZ=0
    g2: LineSegment StartX=310 StartY=-1100 StartZ=0 EndX=310 EndY=0 EndZ=0
    g3: LineSegment StartX=310 StartY=0 StartZ=0 EndX=0 EndY=0 EndZ=0
    g4: LineSegment StartX=102.05 StartY=-7 StartZ=0 EndX=102.05 EndY=-49.9 EndZ=0
    g5: LineSegment StartX=102.05 StartY=-49.9 StartZ=0 EndX=107.05 EndY=-49.9 EndZ=0
    g6: LineSegment StartX=107.05 StartY=-49.9 StartZ=0 EndX=107.05 EndY=-7 EndZ=0
    g7: LineSegment StartX=107.05 StartY=-7 StartZ=0 EndX=102.05 EndY=-7 EndZ=0
  constraints (23):
    c: Coincident(g0,g1)
    c: Coincident(g1,g2)
    c: Coincident(g2,g3)
    c: Coincident(g3,g0)
    c: Vertical(g0)
    c: Vertical(g2)
    c: Horizontal(g1)
    c: Horizontal(g3)
    c: Coincident(g0,g-1)
    c: Coincident(g4,g5)
    c: Coincident(g5,g6)
    c: Coincident(g6,g7)
    c: Coincident(g7,g4)
    c: Vertical(g4)
    c: Vertical(g6)
    c: Horizontal(g5)
    c: Horizontal(g7)
    c: DistanceX(g3,g3) = 310
    c: DistanceY(g0,g0) = 1100
    c: DistanceX(g7,g7) = 5
    c: DistanceY(g6,g6) = 42.9
    c: DistanceX(g-1,g4) = 102.05
    c: DistanceY(g4,g-1) = 7
FEATURE [PartDesign::Pocket] Pocket007
  BaseFeature = -> Pad003
  Direction = (0,0,-1)
  Length = 100
  Length2 = 5
  Midplane = true
  Placement = pos=(0,0,0) rot=(1,0,0;1.5708rad)
  Profile = -> Sketch013
  ReferenceAxis = -> Sketch013 [N_Axis]
  Refine = true
  Suppressed = false
  Type = 0
FEATURE [Sketcher::SketchObject] Sketch014
  ArcFitTolerance = 1e-06
  AttachmentSupport = -> [Pocket007]
  FullyConstrained = false
  MakeInternals = false
  MapMode = 5
  Placement = pos=(107.05,0,0) rot=(0.707107,0,0.707107;3.14159rad)
  sketch-geometry (4):
    g0: LineSegment StartX=21.0275 StartY=47.9 StartZ=0 EndX=-3.47253 EndY=47.9 EndZ=0
    g1: LineSegment StartX=-3.47253 StartY=47.9 StartZ=0 EndX=-3.47253 EndY=9 EndZ=0
    g2: LineSegment StartX=-3.47253 StartY=9 StartZ=0 EndX=21.0275 EndY=9 EndZ=0
    g3: LineSegment StartX=21.0275 StartY=9 StartZ=0 EndX=21.0275 EndY=47.9 EndZ=0
  constraints (11):
    c: Coincident(g0,g1)
    c: Coincident(g1,g2)
    c: Coincident(g2,g3)
    c: Coincident(g3,g0)
    c: Horizontal(g0)
    c: Horizontal(g2)
    c: Vertical(g1)
    c: Vertical(g3)
    c: DistanceY(g3,g3) = 38.9
    c: DistanceY(g-1,g1) = 9
    c: DistanceX(g0,g0) = 24.5
FEATURE [PartDesign::Pocket] Pocket008
  BaseFeature = -> Pocket007
  Direction = (-1,0,2e-16)
  Length = 5
  Length2 = 5
  Placement = pos=(0,0,0) rot=(1,0,0;1.5708rad)
  Profile = -> Sketch014
  ReferenceAxis = -> Sketch014 [N_Axis]
  Refine = true
  Suppressed = false
  Type = 0
FEATURE [Sketcher::SketchObject] Sketch015
  ArcFitTolerance = 1e-06
  AttachmentSupport = -> [Pocket008]
  FullyConstrained = false
  MakeInternals = false
  MapMode = 5
  Placement = pos=(107.05,0,0) rot=(0.707107,0,0.707107;3.14159rad)
  sketch-geometry (4):
    g0: LineSegment StartX=-4.2398 StartY=34.208 StartZ=0 EndX=22.0046 EndY=23.7515 EndZ=0
    g1: LineSegment StartX=22.0046 StartY=23.7515 StartZ=0 EndX=22.0046 EndY=21.5986 EndZ=0
    g2: LineSegment StartX=22.0046 StartY=21.5986 StartZ=0 EndX=-4.2398 EndY=32.0551 EndZ=0
    g3: LineSegment StartX=-4.2398 StartY=32.0551 StartZ=0 EndX=-4.2398 EndY=34.208 EndZ=0
  constraints (8):
    c: Coincident(g0,g1)
    c: Vertical(g1)
    c: Coincident(g1,g2)
    c: Coincident(g2,g3)
    c: Coincident(g3,g0)
    c: Vertical(g3)
    c: Parallel(g2,g0)
    c: Distance(g2,g0) = 2
FEATURE [PartDesign::Pad] Pad004
  BaseFeature = -> Pocket008
  Direction = (1,0,-2e-16)
  Length = 5
  Length2 = 10
  Placement = pos=(0,0,0) rot=(1,0,0;1.5708rad)
  Profile = -> Sketch015
  ReferenceAxis = -> Sketch015 [N_Axis]
  Refine = true
  Reversed = true
  Suppressed = false
  Type = 0
FEATURE [PartDesign::Body] Body002  label="wing spacer 50mm"
  AllowCompound = false
  Group = -> [Sketch012,Pad003,Sketch013,Pocket007,Sketch014,Pocket008,Sketch015,Pad004]
  Origin = -> Origin002
  Tip = -> Pad004
